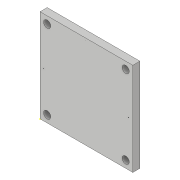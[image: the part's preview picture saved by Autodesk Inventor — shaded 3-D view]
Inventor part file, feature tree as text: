
AUTODESK INVENTOR PART (.ipt)
format: ipt  version: 2019 (Build 230136000, 136)  size: 121,856 bytes
history: native  units: in
note: dims shown in document units (in); Inventor stores cm internally (conversion verified against a paired STEP export)
features: sketch x6, extrude x5
ambient origin geometry x8: Origin, YZ Plane, XZ Plane, XY Plane, X Axis, Y Axis, Z Axis, Center Point
bodies: Solid1 (feature_tree)
feature tree (11):
  extrude  "Extrusion1"  Depth=5.1181in
  extrude  "Extrusion2"  Depth=0.3937in
  extrude  "Extrusion3"  Depth=0.3937in
  extrude  "Extrusion4"  Depth=4.3307in
  extrude  "Extrusion5"  Depth=0.3937in
  sketch  "Sketch6"  dims[d11=0.3937in d12=0.3937in d13=0.3937in d14=0.0in d15=0.0in d16=0.1969in d17=0.1969in d18=0.0039in d19=0.0in d20=0.0in d21=0.1969in d22=0.0039in d23=0.3937in d24=0.0in d25=0.1969in d26=0.0394in d27=0.0394in d28=0.0in d29=0.0in]
  sketch  "Sketch1"  dims[d0=5.1181in d1=5.1181in]
  sketch  "Sketch2"  dims[d2=0.3937in d3=0.0in d4=0.3937in]
  sketch  "Sketch3"  dims[d5=4.3307in d6=0.3937in]
  sketch  "Sketch4"  dims[d7=4.3307in d8=4.3307in]
  sketch  "Sketch5"  dims[d9=4.3307in d10=0.3937in]
